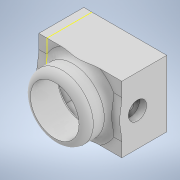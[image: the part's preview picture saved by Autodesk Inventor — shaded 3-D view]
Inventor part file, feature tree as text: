
AUTODESK INVENTOR PART (.ipt)
format: ipt  version: 2020 (Build 240168000, 168)  size: 281,600 bytes
history: native  units: mm
features: sketch x13, extrude x10, projected_geometry x8, other x3, fillet x2, chamfer x2
ambient origin geometry x8: Origin, YZ Plane, XZ Plane, XY Plane, X Axis, Y Axis, Z Axis, Center Point
bodies: Solid1 (feature_tree)
feature tree (38):
  other  "camera and mount block.iam"
  other  "camera mount block.ipt:1"
  other  "dummy camera.ipt:1"
  extrude  "Extrusion1"  Depth=10.0mm TaperAngle=0.0deg
  extrude  "Extrusion2"  Depth=2.0mm
  extrude  "Extrusion3"  Depth=2.0mm TaperAngle=0.0deg
  sketch  "Sketch6"  dims[d13=0.1mm d14=7.0mm d15=0.0mm]
  extrude  "Extrusion4"  Depth=7.0mm TaperAngle=0.0deg
  extrude  "Extrusion5"  Depth=7.0mm TaperAngle=0.0deg
  extrude  "Extrusion6"  Depth=2.0mm
  fillet  "Fillet1"  Radius=2.2mm
  fillet  "Fillet2"  Radius=2.2mm
  chamfer  "Chamfer2"  Distance=2.0mm
  sketch  "Sketch10"  dims[d31=5.0mm d32=2.0mm d33=0.0mm]
  sketch  "Sketch11"  dims[d34=1.5mm d35=2.0mm d36=45.0deg]
  extrude  "Extrusion7"  Depth=2.0mm TaperAngle=0.0deg
  extrude  "Extrusion8"  [1 undecoded]
  extrude  "Extrusion9"  [1 undecoded]
  extrude  "Extrusion10"  [1 undecoded]
  chamfer  "Chamfer3"  [1 undecoded]
  sketch  "Sketch1"  dims[d0=10.0mm d1=10.0mm d2=0.0mm]
  sketch  "Sketch9"  dims[d28=5.0mm d29=2.0mm d30=0.0mm]
  sketch  "Sketch3"  dims[d3=10.0mm d4=0.0mm d5=2.0mm]
  projected_geometry  "Projected Loop1"
  sketch  "Sketch4"  dims[d6=7.0mm d7=0.0mm d8=2.0mm d9=0.0mm]
  projected_geometry  "Projected Loop2"
  sketch  "Sketch5"  dims[d10=0.2mm d11=7.0mm d12=0.0mm]
  projected_geometry  "Projected Loop3"
  sketch  "Sketch7"  dims[d16=2.0mm d17=2.0mm]
  projected_geometry  "Projected Loop4"
  sketch  "Sketch8"  dims[d21=1.0mm d22=2.0mm d23=45.0deg d24=2.2mm d25=0.0mm d26=2.2mm d27=0.0mm]
  projected_geometry  "Projected Loop5"
  projected_geometry  "Projected Loop6"
  projected_geometry  "Projected Loop7"
  sketch  "Sketch12"
  projected_geometry  "Projected Loop8"
  sketch  "Sketch13"
  sketch  "Sketch14"
note: 4 required parameter values undecoded (feature->parameter linkage not recoverable at this tier; creation-order binding heuristic only, values carry confidence <= 0.55)
